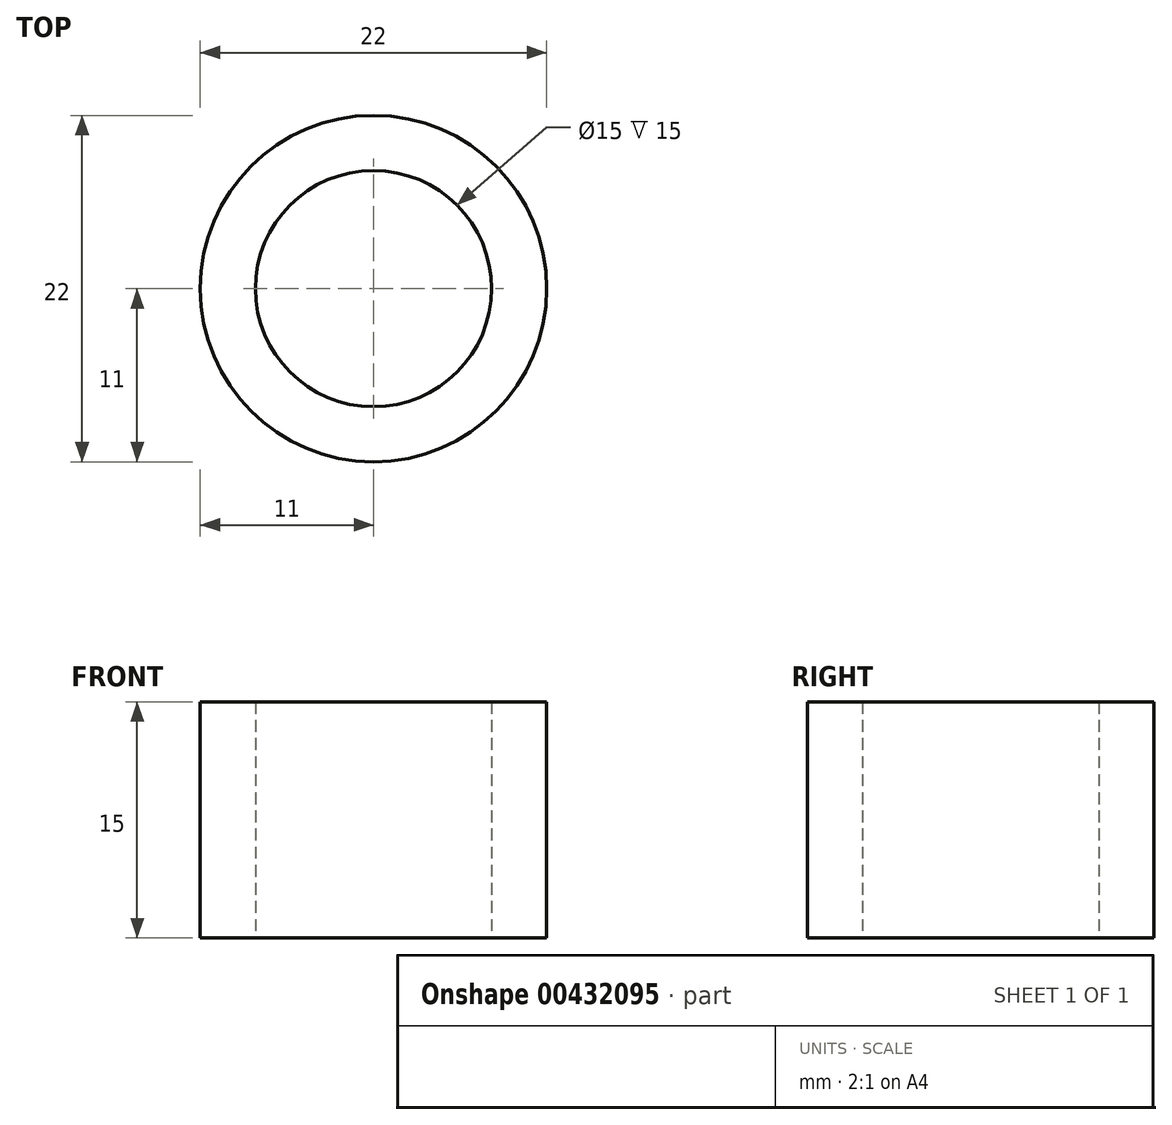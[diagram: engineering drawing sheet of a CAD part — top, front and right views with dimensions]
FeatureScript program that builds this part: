
annotation { "Feature Type Name" : "Feature", "Feature Type Description" : "" }
export const myFeature = defineFeature(function(context is Context, id is Id, definition is map)
    precondition{}
    {
        {
            var Q0;
            Q0=qCreatedBy(makeId("Top.planeOp"),FACE);
            var sketch = newSketch(context, id + "F0", { "sketchPlane" : qUnion([Q0])});
            skCircle(sketch, "E0", {"center": v(0, 0) * mm, "radius": 11 * mm});
            skSolve(sketch);
        }
        {
            var Q0;
            Q0 = qSketchRegion(id + "F0", true);
            extrude(context, id + "F1", {"entities" : qUnion([Q0]), "depth" : 15 * mm});
        }
        {
            var Q0;
            Q0=makeQuery(id+"F1.opExtrude","CAP_FACE",FACE,{"disambiguationData":[OSD([sQuery(id+"F0.wireOp",EDGE,"E0")])],"isStart":true});
            var sketch = newSketch(context, id + "F2", { "sketchPlane" : qUnion([Q0])});
            skPoint(sketch, "E1", {"position": v(0, 0) * mm});
            skSolve(sketch);
        }
        {
            var Q0;
            Q0=sQuery(id+"F2.wireOp",VERTEX,"E1");
            var Q1;
            Q1=makeQuery(id+"F1.opExtrude","SWEPT_BODY",BODY,{"disambiguationData":[OSD([sQuery(id+"F0.wireOp",EDGE,"E0")])]});
            hole(context, id + "F3", {"style" : HoleStyle.SIMPLE, "endStyle" : HoleEndStyle.THROUGH, "holeDiameter" : 15 * mm, "isTappedThrough" : true, "tappedDepth" : 12.7 * mm, "tapClearance" : 3, "locations" : qUnion([Q0]), "scope" : qUnion([Q1])});
        }
    });
